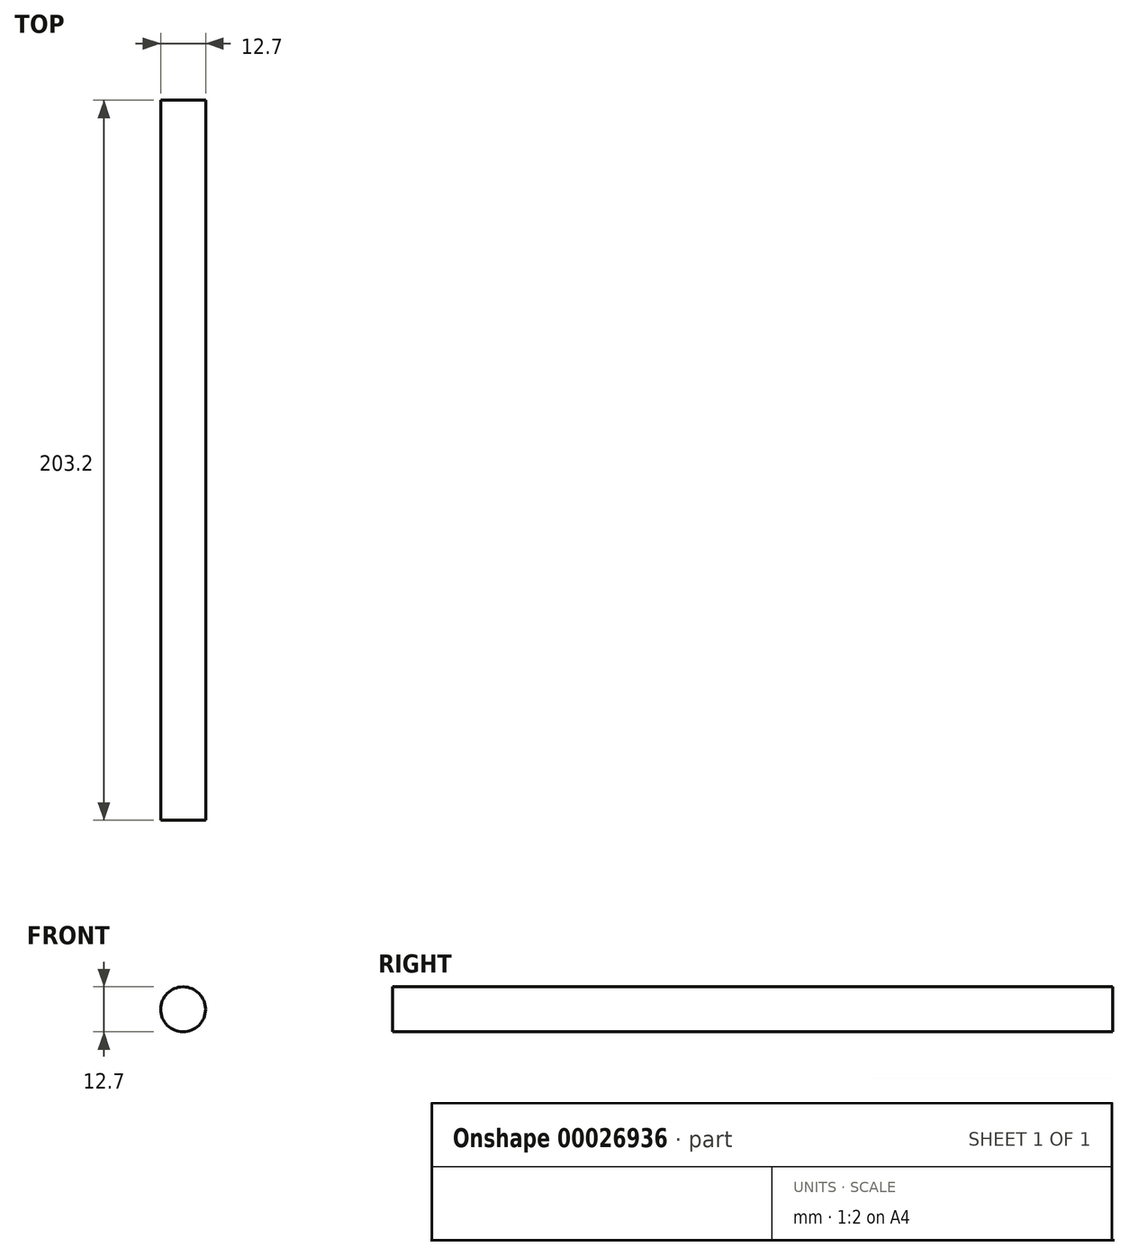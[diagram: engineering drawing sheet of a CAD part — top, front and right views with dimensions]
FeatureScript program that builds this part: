
annotation { "Feature Type Name" : "Feature", "Feature Type Description" : "" }
export const myFeature = defineFeature(function(context is Context, id is Id, definition is map)
    precondition{}
    {
        {
            var Q0;
            Q0=qCreatedBy(makeId("Front.planeOp"),FACE);
            var sketch = newSketch(context, id + "F0", { "sketchPlane" : qUnion([Q0])});
            skCircle(sketch, "E0", {"center": v(-1.96, 2.78) * mm, "radius": 6.35 * mm});
            skSolve(sketch);
        }
        {
            var Q0;
            Q0=makeQuery(id+"F0.imprint","IMPRINT",FACE,{"disambiguationData":[TD([[makeQuery(id+"F0.imprint","IMPRINT",EDGE,{"derivedFrom":sQuery(id+"F0.wireOp",EDGE,"E0")}),1.0]])]});
            extrude(context, id + "F1", {"entities" : qUnion([Q0]), "depth" : 203.2 * mm});
        }
    });
